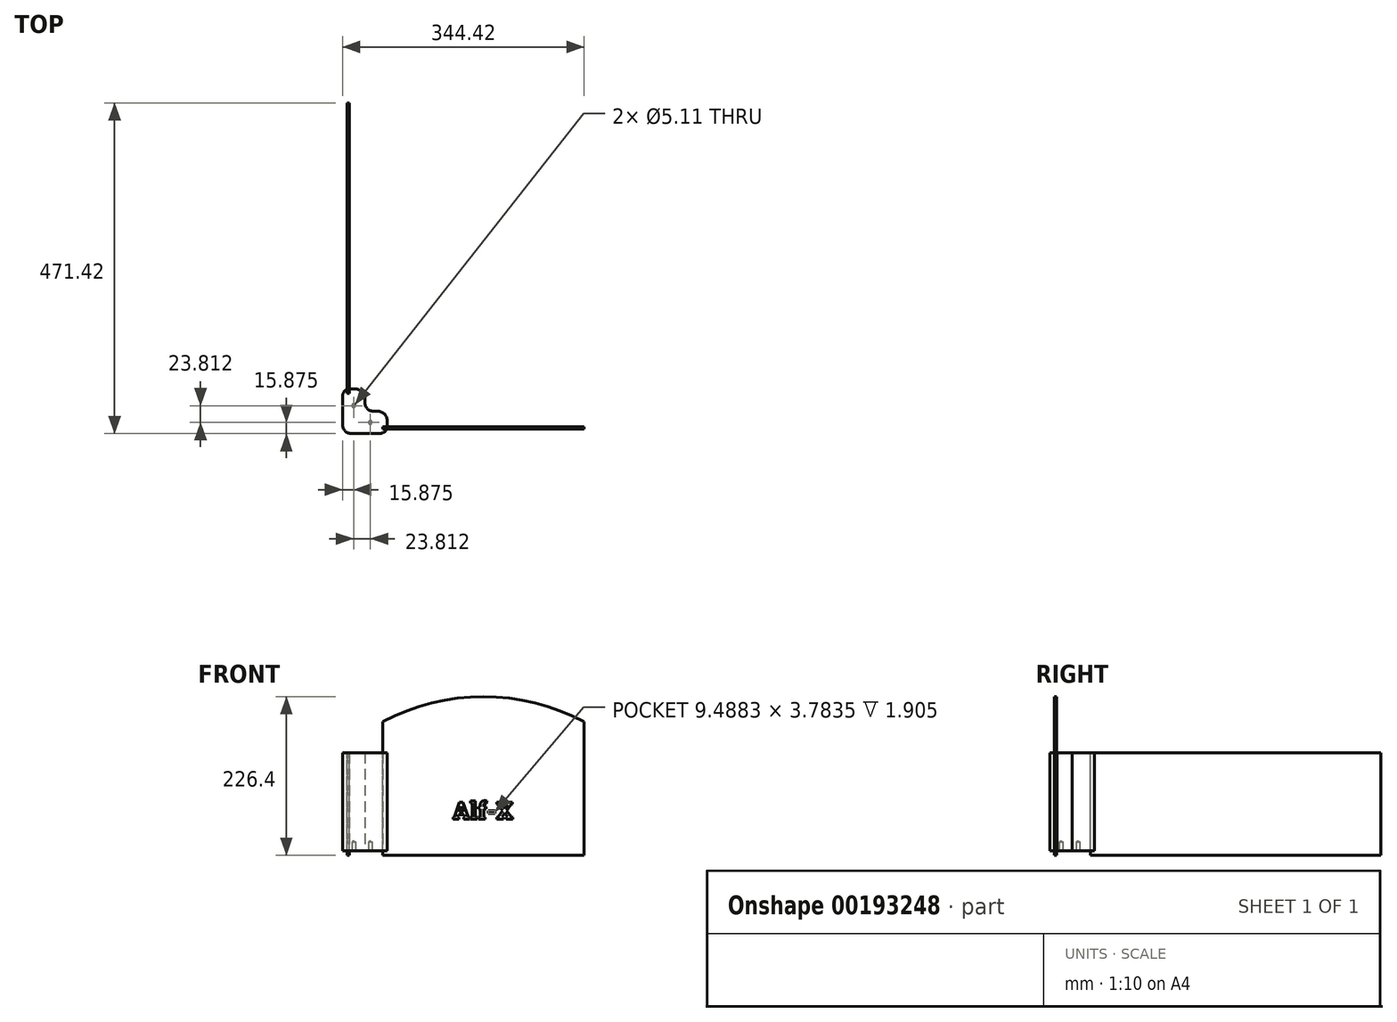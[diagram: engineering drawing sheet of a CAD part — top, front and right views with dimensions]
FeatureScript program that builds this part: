
annotation { "Feature Type Name" : "Feature", "Feature Type Description" : "" }
export const myFeature = defineFeature(function(context is Context, id is Id, definition is map)
    precondition{}
    {
        {
            var Q0;
            Q0=qCreatedBy(makeId("Top.planeOp"),FACE);
            var sketch = newSketch(context, id + "F0", { "sketchPlane" : qUnion([Q0])});
            skLineSegment(sketch, "E0.bottom", {"start": v(31.75, -31.75) * mm, "end": v(-31.75, -31.75) * mm});
            skLineSegment(sketch, "E0.top", {"start": v(0, 31.75) * mm, "end": v(-22.1, 31.75) * mm});
            skLineSegment(sketch, "E0.left", {"start": v(31.75, -31.75) * mm, "end": v(31.75, -25.4) * mm});
            skLineSegment(sketch, "E0.right", {"start": v(-31.75, -31.75) * mm, "end": v(-31.75, 31.75) * mm});
            skPoint(sketch, "E0.middle", {"position": v(0, 0) * mm});
            skLineSegment(sketch, "E1", {"start": v(0, 31.75) * mm, "end": v(0, 0) * mm});
            skLineSegment(sketch, "E2", {"start": v(0, 0) * mm, "end": v(31.75, 0) * mm});
            skPoint(sketch, "E3.orphan", {"position": v(31.75, 31.75) * mm});
            skLineSegment(sketch, "E4.trimOffspring", {"start": v(-25.4, 31.75) * mm, "end": v(-31.75, 31.75) * mm});
            skLineSegment(sketch, "E5.trimOffspring", {"start": v(31.75, -22.1) * mm, "end": v(31.75, 0) * mm});
            skLineSegment(sketch, "E6", {"start": v(31.75, -25.4) * mm, "end": v(25.4, -25.4) * mm});
            skLineSegment(sketch, "E7", {"start": v(25.4, -25.4) * mm, "end": v(25.4, -22.1) * mm});
            skLineSegment(sketch, "E8", {"start": v(25.4, -22.1) * mm, "end": v(31.75, -22.1) * mm});
            skLineSegment(sketch, "E9", {"start": v(-25.4, 31.75) * mm, "end": v(-25.4, 25.4) * mm});
            skLineSegment(sketch, "E10", {"start": v(-25.4, 25.4) * mm, "end": v(-22.1, 25.4) * mm});
            skLineSegment(sketch, "E11", {"start": v(-22.1, 25.4) * mm, "end": v(-22.1, 31.75) * mm});
            skSolve(sketch);
        }
        {
            var Q0;
            Q0 = qSketchRegion(id + "F0", true);
            extrude(context, id + "F1", {"entities" : qUnion([Q0]), "depth" : 139.7 * mm});
        }
        {
            var Q0;
            Q0=makeQuery(id+"F1.opExtrude","SWEPT_EDGE",EDGE,{"disambiguationData":[OSD([sQuery(id+"F0.wireOp",EDGE,"E1"),sQuery(id+"F0.wireOp",EDGE,"E2")])]});
            var Q1;
            Q1=makeQuery(id+"F1.opExtrude","SWEPT_EDGE",EDGE,{"disambiguationData":[OSD([sQuery(id+"F0.wireOp",EDGE,"E0.bottom"),sQuery(id+"F0.wireOp",EDGE,"E0.right")])]});
            var Q2;
            Q2=makeQuery(id+"F1.opExtrude","SWEPT_EDGE",EDGE,{"disambiguationData":[OSD([sQuery(id+"F0.wireOp",EDGE,"E0.right"),sQuery(id+"F0.wireOp",EDGE,"E4.trimOffspring")])]});
            var Q3;
            Q3=makeQuery(id+"F1.opExtrude","SWEPT_EDGE",EDGE,{"disambiguationData":[OSD([sQuery(id+"F0.wireOp",EDGE,"E0.top"),sQuery(id+"F0.wireOp",EDGE,"E1")])]});
            var Q4;
            Q4=makeQuery(id+"F1.opExtrude","SWEPT_EDGE",EDGE,{"disambiguationData":[OSD([sQuery(id+"F0.wireOp",EDGE,"E2"),sQuery(id+"F0.wireOp",EDGE,"E5.trimOffspring")])]});
            var Q5;
            Q5=makeQuery(id+"F1.opExtrude","SWEPT_EDGE",EDGE,{"disambiguationData":[OSD([sQuery(id+"F0.wireOp",EDGE,"E0.bottom"),sQuery(id+"F0.wireOp",EDGE,"E0.left")])]});
            fillet(context, id + "F2", {"entities" : qUnion([Q0, Q1, Q2, Q3, Q4, Q5]), "radius" : 12.7 * mm, "tangentPropagation" : true, "allowEdgeOverflow" : false});
        }
        {
            var Q0;
            Q0=makeQuery(id+"F1.opExtrude","CAP_FACE",FACE,{"disambiguationData":[OSD([sQuery(id+"F0.wireOp",EDGE,"E0.bottom"),sQuery(id+"F0.wireOp",EDGE,"E0.top"),sQuery(id+"F0.wireOp",EDGE,"E0.left"),sQuery(id+"F0.wireOp",EDGE,"E0.right"),sQuery(id+"F0.wireOp",EDGE,"E1"),sQuery(id+"F0.wireOp",EDGE,"E2"),sQuery(id+"F0.wireOp",EDGE,"i84V2whz-ty2n-i2ic-8My6-kg7npR0pECNW.top"),sQuery(id+"F0.wireOp",EDGE,"i84V2whz-ty2n-i2ic-8My6-kg7npR0pECNW.left"),sQuery(id+"F0.wireOp",EDGE,"i84V2whz-ty2n-i2ic-8My6-kg7npR0pECNW.right"),sQuery(id+"F0.wireOp",EDGE,"5U4PjdKC-8jsH-slO9-53Rf-qQwJecpSyyx8.bottom"),sQuery(id+"F0.wireOp",EDGE,"5U4PjdKC-8jsH-slO9-53Rf-qQwJecpSyyx8.top"),sQuery(id+"F0.wireOp",EDGE,"5U4PjdKC-8jsH-slO9-53Rf-qQwJecpSyyx8.right"),sQuery(id+"F0.wireOp",EDGE,"E4.trimOffspring"),sQuery(id+"F0.wireOp",EDGE,"E5.trimOffspring")])],"isStart":true});
            var sketch = newSketch(context, id + "F3", { "sketchPlane" : qUnion([Q0])});
            skLineSegment(sketch, "E12", {"start": v(-15.87, -31.75) * mm, "end": v(-15.87, 15.87) * mm});
            skLineSegment(sketch, "E13", {"start": v(31.75, 15.88) * mm, "end": v(-15.87, 15.87) * mm});
            skPoint(sketch, "E14", {"position": v(-15.87, -7.94) * mm});
            skPoint(sketch, "E15", {"position": v(7.94, 15.88) * mm});
            skLineSegment(sketch, "E16", {"start": v(24.55, 31.75) * mm, "end": v(24.55, 0) * mm, "construction": true});
            skLineSegment(sketch, "E17", {"start": v(0, -19.94) * mm, "end": v(-31.75, -19.94) * mm, "construction": true});
            skPoint(sketch, "E18", {"position": v(24.55, 15.88) * mm});
            skPoint(sketch, "E19", {"position": v(-15.88, -19.94) * mm});
            skSolve(sketch);
        }
        {
            var Q0;
            Q0=sQuery(id+"F3.wireOp",VERTEX,"E14");
            var Q1;
            Q1=sQuery(id+"F3.wireOp",VERTEX,"E15");
            var Q2;
            Q2=makeQuery(id+"F1.opExtrude","SWEPT_BODY",BODY,{"disambiguationData":[OSD([sQuery(id+"F0.wireOp",EDGE,"E0.bottom"),sQuery(id+"F0.wireOp",EDGE,"E0.top"),sQuery(id+"F0.wireOp",EDGE,"E0.left"),sQuery(id+"F0.wireOp",EDGE,"E0.right"),sQuery(id+"F0.wireOp",EDGE,"E1"),sQuery(id+"F0.wireOp",EDGE,"E2"),sQuery(id+"F0.wireOp",EDGE,"i84V2whz-ty2n-i2ic-8My6-kg7npR0pECNW.top"),sQuery(id+"F0.wireOp",EDGE,"i84V2whz-ty2n-i2ic-8My6-kg7npR0pECNW.left"),sQuery(id+"F0.wireOp",EDGE,"i84V2whz-ty2n-i2ic-8My6-kg7npR0pECNW.right"),sQuery(id+"F0.wireOp",EDGE,"5U4PjdKC-8jsH-slO9-53Rf-qQwJecpSyyx8.bottom"),sQuery(id+"F0.wireOp",EDGE,"5U4PjdKC-8jsH-slO9-53Rf-qQwJecpSyyx8.top"),sQuery(id+"F0.wireOp",EDGE,"5U4PjdKC-8jsH-slO9-53Rf-qQwJecpSyyx8.right"),sQuery(id+"F0.wireOp",EDGE,"E4.trimOffspring"),sQuery(id+"F0.wireOp",EDGE,"E5.trimOffspring")])]});
            hole(context, id + "F4", {"style" : HoleStyle.SIMPLE, "endStyle" : HoleEndStyle.BLIND, "standardTappedOrClearance" : lookupTablePath({ "standard" : "ANSI", "engagement" : "75%", "pitch" : "20 tpi", "size" : "1/4", "type" : "Tapped" }), "standardBlindInLast" : lookupTablePath({ "standard" : "ANSI", "engagement" : "75%", "pitch" : "20 tpi", "size" : "1/4", "type" : "Tapped" }), "holeDiameter" : 5.1 * mm, "holeDepth" : 12.7 * mm, "locations" : qUnion([Q0, Q1]), "scope" : qUnion([Q2]), "majorDiameter" : 6.35 * mm});
        }
        {
            var Q0;
            Q0=makeQuery(id+"F1.opExtrude","CAP_FACE",FACE,{"disambiguationData":[OSD([sQuery(id+"F0.wireOp",EDGE,"E0.bottom"),sQuery(id+"F0.wireOp",EDGE,"E0.top"),sQuery(id+"F0.wireOp",EDGE,"E0.left"),sQuery(id+"F0.wireOp",EDGE,"E0.right"),sQuery(id+"F0.wireOp",EDGE,"E1"),sQuery(id+"F0.wireOp",EDGE,"E2"),sQuery(id+"F0.wireOp",EDGE,"E4.trimOffspring"),sQuery(id+"F0.wireOp",EDGE,"E5.trimOffspring"),sQuery(id+"F0.wireOp",EDGE,"E6"),sQuery(id+"F0.wireOp",EDGE,"E7"),sQuery(id+"F0.wireOp",EDGE,"E8"),sQuery(id+"F0.wireOp",EDGE,"E9"),sQuery(id+"F0.wireOp",EDGE,"E10"),sQuery(id+"F0.wireOp",EDGE,"E11")])],"isStart":false});
            var sketch = newSketch(context, id + "F5", { "sketchPlane" : qUnion([Q0])});
            skLineSegment(sketch, "E20.bottom", {"start": v(-22.16, 25.65) * mm, "end": v(-25.34, 25.65) * mm});
            skLineSegment(sketch, "E20.top", {"start": v(-22.16, 439.67) * mm, "end": v(-25.34, 439.67) * mm});
            skLineSegment(sketch, "E20.left", {"start": v(-22.16, 25.65) * mm, "end": v(-22.16, 439.67) * mm});
            skLineSegment(sketch, "E20.right", {"start": v(-25.34, 25.65) * mm, "end": v(-25.34, 439.67) * mm});
            skPoint(sketch, "E20.middle", {"position": v(-23.75, 232.66) * mm});
            skSolve(sketch);
        }
        {
            var Q0;
            Q0 = qSketchRegion(id + "F5", true);
            extrude(context, id + "F6", {"entities" : qUnion([Q0]), "oppositeDirection" : true, "depth" : 146.05 * mm});
        }
        {
            var Q0;
            Q0=makeQuery(id+"F1.opExtrude","CAP_FACE",FACE,{"disambiguationData":[OSD([sQuery(id+"F0.wireOp",EDGE,"E0.bottom"),sQuery(id+"F0.wireOp",EDGE,"E0.top"),sQuery(id+"F0.wireOp",EDGE,"E0.left"),sQuery(id+"F0.wireOp",EDGE,"E0.right"),sQuery(id+"F0.wireOp",EDGE,"E1"),sQuery(id+"F0.wireOp",EDGE,"E2"),sQuery(id+"F0.wireOp",EDGE,"E4.trimOffspring"),sQuery(id+"F0.wireOp",EDGE,"E5.trimOffspring"),sQuery(id+"F0.wireOp",EDGE,"E6"),sQuery(id+"F0.wireOp",EDGE,"E7"),sQuery(id+"F0.wireOp",EDGE,"E8"),sQuery(id+"F0.wireOp",EDGE,"E9"),sQuery(id+"F0.wireOp",EDGE,"E10"),sQuery(id+"F0.wireOp",EDGE,"E11")])],"isStart":false});
            var sketch = newSketch(context, id + "F7", { "sketchPlane" : qUnion([Q0])});
            skLineSegment(sketch, "E21.bottom", {"start": v(25.65, -25.34) * mm, "end": v(312.67, -25.34) * mm});
            skLineSegment(sketch, "E21.top", {"start": v(25.65, -22.16) * mm, "end": v(312.67, -22.16) * mm});
            skLineSegment(sketch, "E21.left", {"start": v(25.65, -25.34) * mm, "end": v(25.65, -22.16) * mm});
            skLineSegment(sketch, "E21.right", {"start": v(312.67, -25.34) * mm, "end": v(312.67, -22.16) * mm});
            skPoint(sketch, "E21.middle", {"position": v(169.16, -23.75) * mm});
            skSolve(sketch);
        }
        {
            var Q0;
            Q0=makeQuery(id+"F7.imprint","IMPRINT",FACE,{"disambiguationData":[TD([[makeQuery(id+"F7.imprint","IMPRINT",EDGE,{"derivedFrom":sQuery(id+"F7.wireOp",EDGE,"E21.bottom")}),1.0]])]});
            extrude(context, id + "F8", {"entities" : qUnion([Q0]), "oppositeDirection" : true, "depth" : 146.05 * mm});
        }
        {
            var Q0;
            Q0=makeQuery(id+"F8.opExtrude","SWEPT_FACE",FACE,{"disambiguationData":[OSD([sQuery(id+"F7.wireOp",EDGE,"E21.bottom")])]});
            var sketch = newSketch(context, id + "F9", { "sketchPlane" : qUnion([Q0])});
            skLineSegment(sketch, "E22", {"start": v(25.65, 21.8) * mm, "end": v(312.67, 21.8) * mm});
            skText(sketch, "E23", { "text": "Alf-X", "fontName": "RobotoSlab-Bold.ttf"});
            const initialGuessF9  = {"E23": [0.12517, 0.04505, 1, 0, 0.0248]};
            skSetInitialGuess(sketch, initialGuessF9);
            skSolve(sketch);
        }
        {
            var Q0;
            Q0 = qSketchRegion(id + "F9", true);
            extrude(context, id + "F10", {"entities" : qUnion([Q0]), "operationType" : NewBodyOperationType.REMOVE, "oppositeDirection" : true, "depth" : 1.9 * mm});
        }
        {
            var Q0;
            {var subQ0=sQuery(id+"F7.wireOp",EDGE,"E21.left");var subQ3=sQuery(id+"F7.wireOp",EDGE,"E21.bottom");Q0=makeQuery(id+"F10.boolean.opBoolean","SPLIT",FACE,{"disambiguationData":[TD([makeQuery(id+"F8.opExtrude","SWEPT_FACE",FACE,{"disambiguationData":[OSD([subQ0])]})])],"derivedFrom":makeQuery(id+"F8.opExtrude","SWEPT_FACE",FACE,{"disambiguationData":[OSD([subQ3])]})});}
            var sketch = newSketch(context, id + "F11", { "sketchPlane" : qUnion([Q0])});
            skLineSegment(sketch, "E24.0", {"start": v(25.65, 139.7) * mm, "end": v(312.67, 139.7) * mm});
            skLineSegment(sketch, "E25", {"start": v(25.65, 139.7) * mm, "end": v(25.65, 184.15) * mm});
            skLineSegment(sketch, "E26", {"start": v(312.67, 139.7) * mm, "end": v(312.67, 184.15) * mm});
            skArc(sketch, "E27", {"start": v(312.67, 184.15) * mm, "mid": v(169.16, 220.05) * mm, "end": v(25.65, 184.15) * mm});
            skSolve(sketch);
        }
        {
            var Q0;
            Q0 = qSketchRegion(id + "F11", true);
            var Q1;
            Q1=makeQuery(id+"F8.opExtrude","SWEPT_FACE",FACE,{"disambiguationData":[OSD([sQuery(id+"F7.wireOp",EDGE,"E21.top")])]});
            extrude(context, id + "F12", {"entities" : qUnion([Q0]), "operationType" : NewBodyOperationType.ADD, "endBound" : BoundingType.UP_TO_SURFACE, "oppositeDirection" : true, "endBoundEntityFace" : qUnion([Q1]), "depth" : 25.4 * mm});
        }
    });
